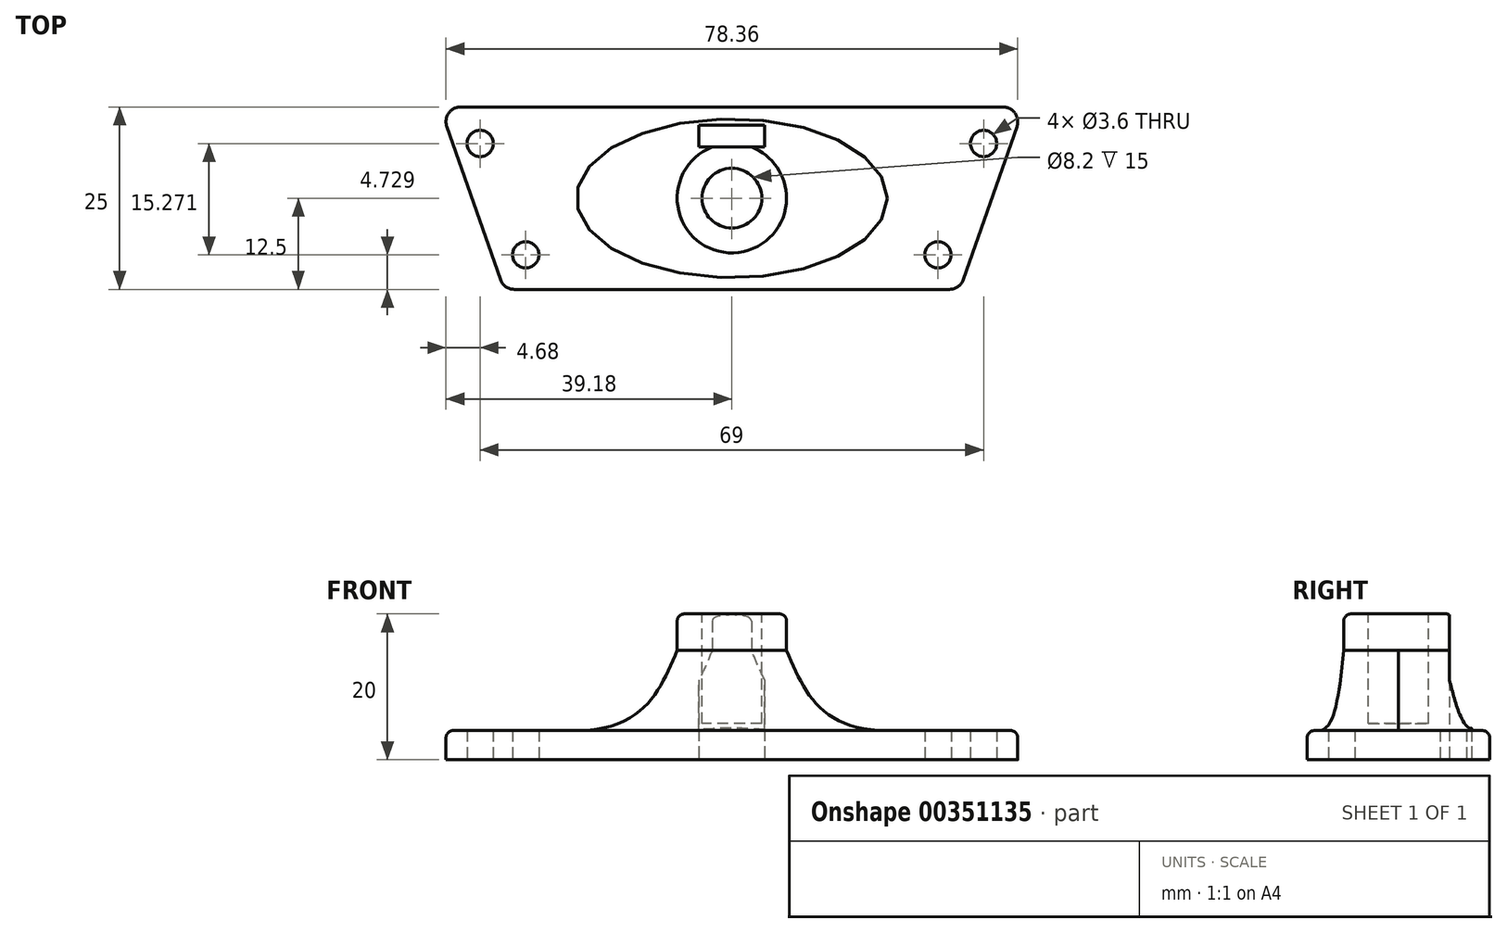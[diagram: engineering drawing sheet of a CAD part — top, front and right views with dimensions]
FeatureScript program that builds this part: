
annotation { "Feature Type Name" : "Feature", "Feature Type Description" : "" }
export const myFeature = defineFeature(function(context is Context, id is Id, definition is map)
    precondition{}
    {
        {
            var Q0;
            Q0=qCreatedBy(makeId("Top.planeOp"),FACE);
            var sketch = newSketch(context, id + "F0", { "sketchPlane" : qUnion([Q0])});
            skLineSegment(sketch, "E0", {"start": v(-37.18, 12.5) * mm, "end": v(37.18, 12.5) * mm});
            skLineSegment(sketch, "E1", {"start": v(39.07, 9.84) * mm, "end": v(31.72, -11.16) * mm});
            skLineSegment(sketch, "E2", {"start": v(29.83, -12.5) * mm, "end": v(-29.83, -12.5) * mm});
            skLineSegment(sketch, "E3", {"start": v(-31.72, -11.16) * mm, "end": v(-39.07, 9.84) * mm});
            skCircle(sketch, "E4", {"center": v(-34.5, 7.5) * mm, "radius": 1.8 * mm});
            skCircle(sketch, "E5", {"center": v(-28.25, -7.77) * mm, "radius": 1.8 * mm});
            skCircle(sketch, "E6", {"center": v(34.5, 7.5) * mm, "radius": 1.8 * mm});
            skCircle(sketch, "E7", {"center": v(28.25, -7.77) * mm, "radius": 1.8 * mm});
            skPoint(sketch, "E8.visualSharp", {"position": v(40, 12.5) * mm});
            skArc(sketch, "E8.filletArc", {"start": v(39.07, 9.84) * mm, "mid": v(38.81, 11.66) * mm, "end": v(37.18, 12.5) * mm});
            skPoint(sketch, "E9.visualSharp", {"position": v(31.25, -12.5) * mm});
            skArc(sketch, "E9.filletArc", {"start": v(29.83, -12.5) * mm, "mid": v(30.99, -12.13) * mm, "end": v(31.72, -11.16) * mm});
            skPoint(sketch, "E10.visualSharp", {"position": v(-31.25, -12.5) * mm});
            skArc(sketch, "E10.filletArc", {"start": v(-31.72, -11.16) * mm, "mid": v(-30.99, -12.13) * mm, "end": v(-29.83, -12.5) * mm});
            skPoint(sketch, "E11.visualSharp", {"position": v(-40, 12.5) * mm});
            skArc(sketch, "E11.filletArc", {"start": v(-37.18, 12.5) * mm, "mid": v(-38.81, 11.66) * mm, "end": v(-39.07, 9.84) * mm});
            skSolve(sketch);
        }
        {
            var Q0;
            Q0 = qSketchRegion(id + "F0", true);
            extrude(context, id + "F1", {"entities" : qUnion([Q0]), "depth" : 4 * mm});
        }
        {
            var Q0;
            {var subQ0=sQuery(id+"F0.wireOp",EDGE,"E8.filletArc");var subQ1=sQuery(id+"F0.wireOp",EDGE,"E7");var subQ2=sQuery(id+"F0.wireOp",EDGE,"E6");var subQ3=sQuery(id+"F0.wireOp",EDGE,"E5");var subQ4=sQuery(id+"F0.wireOp",EDGE,"E4");var subQ5=sQuery(id+"F0.wireOp",EDGE,"E9.filletArc");var subQ6=sQuery(id+"F0.wireOp",EDGE,"E0");var subQ7=sQuery(id+"F0.wireOp",EDGE,"E3");var subQ8=sQuery(id+"F0.wireOp",EDGE,"E1");var subQ9=sQuery(id+"F0.wireOp",EDGE,"E2");var subQ10=sQuery(id+"F0.wireOp",EDGE,"E10.filletArc");var subQ11=sQuery(id+"F0.wireOp",EDGE,"E11.filletArc");Q0=makeQuery(id+"F404k3TC5tdL10r_1.boolean.opBoolean","SPLIT",FACE,{"disambiguationData":[TD([makeQuery(id+"F1.opExtrude","SWEPT_FACE",FACE,{"disambiguationData":[OSD([subQ6])]})])],"derivedFrom":makeQuery(id+"F1.opExtrude","CAP_FACE",FACE,{"disambiguationData":[OSD([subQ6,subQ8,subQ9,subQ7,subQ4,subQ3,subQ2,subQ1,subQ0,subQ5,subQ10,subQ11])],"isStart":false})});}
            var sketch = newSketch(context, id + "F2", { "sketchPlane" : qUnion([Q0])});
            skEllipse(sketch, "E12", {"center": v(0, 0) * mm, "majorRadius": 21.29 * mm, "minorRadius": 10.89 * mm, "majorAxis": v(1, 0)});
            skSolve(sketch);
        }
        {
            var Q0;
            Q0=makeQuery(id+"F1.opExtrude","CAP_EDGE",EDGE,{"disambiguationData":[OSD([sQuery(id+"F0.wireOp",EDGE,"E1")])],"isStart":false});
            var Q1;
            Q1=makeQuery(id+"F1CGGRwKsAl5Pjg_1.boolean.opBoolean","MERGE",EDGE,{"derivedFrom":[makeQuery(id+"F404k3TC5tdL10r_1.opExtrude","CAP_EDGE",EDGE,{"disambiguationData":[OSD([sQuery(id+"F276eezdKuVL19V_1.wireOp",EDGE,"3HG2ZnaV-9RCq-uJFL-7UCv-jKWA1IPvCyHm")])],"isStart":false}),makeQuery(id+"F1CGGRwKsAl5Pjg_1.opLoft","MID_CAP_EDGE",EDGE,{"disambiguationData":[OSD([sQuery(id+"F5zLKOWcRKZyHUO_1.wireOp",EDGE,"Q2qZblnE-h02P-mmj6-HxCN-xBIc61h3tOFj"),sQuery(id+"F2.wireOp",EDGE,"E12")])],"capPos":1.0})]});
            fillet(context, id + "F3", {"entities" : qUnion([Q0, Q1]), "radius" : 1 * mm, "tangentPropagation" : true, "allowEdgeOverflow" : false});
        }
        {
            var Q0;
            Q0=qCreatedBy(makeId("Top.planeOp"),FACE);
            cPlane(context, id + "F4", {"entities" : qUnion([Q0]), "cplaneType" : CPlaneType.OFFSET, "offset" : 15 * mm, "width" : 150 * mm, "height" : 150 * mm});
        }
        {
            var Q0;
            Q0=qCreatedBy(id+"F4.planeOp",FACE);
            var sketch = newSketch(context, id + "F5", { "sketchPlane" : qUnion([Q0])});
            skCircle(sketch, "E13", {"center": v(0, 0) * mm, "radius": 7.5 * mm});
            skSolve(sketch);
        }
        {
            var Q0;
            Q0 = qSketchRegion(id + "F5", true);
            extrude(context, id + "F6", {"entities" : qUnion([Q0]), "depth" : 5 * mm});
        }
        {
            var Q1;
            Q1 = qSketchRegion(id + "F2", true);
            var Q2;
            Q2 = qSketchRegion(id + "F5", true);
            loft(context, id + "F7", {"operationType" : NewBodyOperationType.ADD, "startCondition" : LoftEndDerivativeType.TANGENT_TO_PROFILE, "startMagnitude" : 2, "sheetProfilesArray" : [{ "sheetProfileEntities" : qUnion([Q1]) }, { "sheetProfileEntities" : qUnion([Q2]) }]});
        }
        {
            var Q0;
            Q0=makeQuery(id+"F6.opExtrude","CAP_FACE",FACE,{"disambiguationData":[OSD([sQuery(id+"F5.wireOp",EDGE,"E13")])],"isStart":false});
            fillet(context, id + "F8", {"entities" : qUnion([Q0]), "radius" : 1 * mm, "tangentPropagation" : true, "allowEdgeOverflow" : false});
        }
        {
            var Q0;
            Q0=makeQuery(id+"F6.opExtrude","CAP_FACE",FACE,{"disambiguationData":[OSD([sQuery(id+"F5.wireOp",EDGE,"E13")])],"isStart":false});
            var sketch = newSketch(context, id + "F9", { "sketchPlane" : qUnion([Q0])});
            skCircle(sketch, "E14", {"center": v(0, 0) * mm, "radius": 4.1 * mm});
            skSolve(sketch);
        }
        {
            var Q0;
            Q0 = qSketchRegion(id + "F9", true);
            extrude(context, id + "F10", {"entities" : qUnion([Q0]), "operationType" : NewBodyOperationType.REMOVE, "oppositeDirection" : true, "depth" : 15 * mm});
        }
        {
            var Q0;
            Q0=makeQuery(id+"F1.opExtrude","CAP_FACE",FACE,{"disambiguationData":[OSD([sQuery(id+"F0.wireOp",EDGE,"E0"),sQuery(id+"F0.wireOp",EDGE,"E1"),sQuery(id+"F0.wireOp",EDGE,"E2"),sQuery(id+"F0.wireOp",EDGE,"E3"),sQuery(id+"F0.wireOp",EDGE,"E4"),sQuery(id+"F0.wireOp",EDGE,"E5"),sQuery(id+"F0.wireOp",EDGE,"E6"),sQuery(id+"F0.wireOp",EDGE,"E7"),sQuery(id+"F0.wireOp",EDGE,"E8.filletArc"),sQuery(id+"F0.wireOp",EDGE,"E9.filletArc"),sQuery(id+"F0.wireOp",EDGE,"E10.filletArc"),sQuery(id+"F0.wireOp",EDGE,"E11.filletArc")])],"isStart":true});
            var sketch = newSketch(context, id + "F11", { "sketchPlane" : qUnion([Q0])});
            skLineSegment(sketch, "E15.bottom", {"start": v(-4.5, -7) * mm, "end": v(4.5, -7) * mm});
            skLineSegment(sketch, "E15.top", {"start": v(-4.5, -10) * mm, "end": v(4.5, -10) * mm});
            skLineSegment(sketch, "E15.left", {"start": v(-4.5, -7) * mm, "end": v(-4.5, -10) * mm});
            skLineSegment(sketch, "E15.right", {"start": v(4.5, -7) * mm, "end": v(4.5, -10) * mm});
            skSolve(sketch);
        }
        {
            var Q0;
            Q0 = qSketchRegion(id + "F11", true);
            extrude(context, id + "F12", {"entities" : qUnion([Q0]), "operationType" : NewBodyOperationType.REMOVE, "endBound" : BoundingType.THROUGH_ALL, "oppositeDirection" : true, "depth" : 25 * mm});
        }
    });
